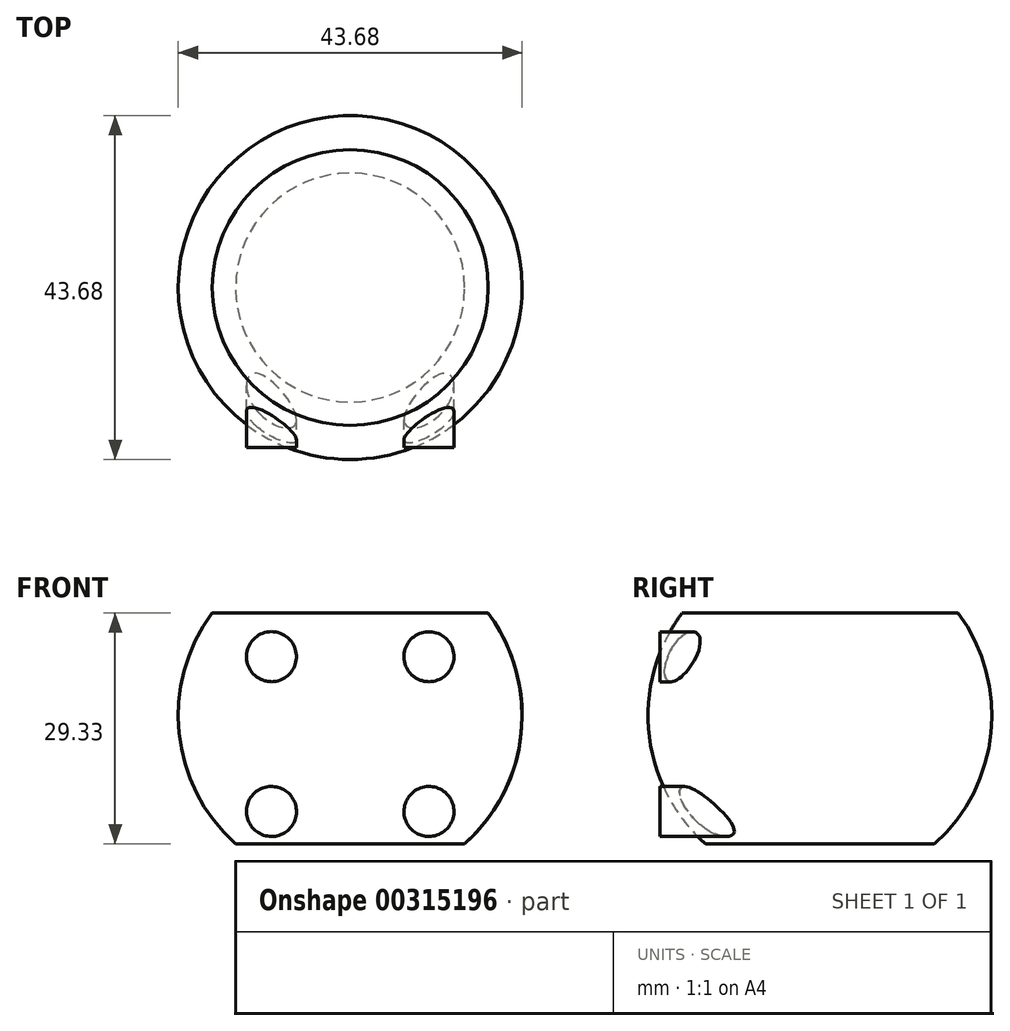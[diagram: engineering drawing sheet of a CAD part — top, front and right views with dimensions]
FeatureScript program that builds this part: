
annotation { "Feature Type Name" : "Feature", "Feature Type Description" : "" }
export const myFeature = defineFeature(function(context is Context, id is Id, definition is map)
    precondition{}
    {
        {
            var Q0;
            Q0=qCreatedBy(makeId("Front.planeOp"),FACE);
            var sketch = newSketch(context, id + "F0", { "sketchPlane" : qUnion([Q0])});
            skArc(sketch, "E0", {"start": v(-17.52, 13.04) * mm, "mid": v(-21.73, -2.2) * mm, "end": v(-14.55, -16.3) * mm});
            skLineSegment(sketch, "E1", {"start": v(-17.52, 13.04) * mm, "end": v(17.52, 13.04) * mm});
            skLineSegment(sketch, "E2", {"start": v(0, 33.05) * mm, "end": v(0, -36.53) * mm});
            skPoint(sketch, "E2.endSnap0", {"position": v(0, 13.04) * mm});
            skLineSegment(sketch, "E3", {"start": v(-14.55, -16.3) * mm, "end": v(14.55, -16.3) * mm});
            skArc(sketch, "E4.trimOffspring", {"start": v(14.55, -16.3) * mm, "mid": v(21.73, -2.2) * mm, "end": v(17.52, 13.04) * mm});
            skPoint(sketch, "E5.center.orphan", {"position": v(-8.7, -12.61) * mm});
            skPoint(sketch, "E6.center.orphan", {"position": v(8.7, -12.61) * mm});
            skSolve(sketch);
        }
        {
            var Q0;
            {var subQ1=sQuery(id+"F0.wireOp",EDGE,"E0");Q0=makeQuery(id+"F0.imprint","IMPRINT",FACE,{"disambiguationData":[TD([[makeQuery(id+"F0.imprint","IMPRINT",EDGE,{"derivedFrom":subQ1}),1.0]])]});}
            var Q1;
            Q1=sQuery(id+"F0.wireOp",EDGE,"E2");
            revolve(context, id + "F1", {"entities" : qUnion([Q0]), "axis" : qUnion([Q1]), "revolveType" : RevolveType.FULL});
        }
        {
            var Q0;
            Q0=qCreatedBy(makeId("Front.planeOp"),FACE);
            var sketch = newSketch(context, id + "F2", { "sketchPlane" : qUnion([Q0])});
            skCircle(sketch, "E7", {"center": v(-10, -12.18) * mm, "radius": 3.18 * mm});
            skCircle(sketch, "E8", {"center": v(10, -12.18) * mm, "radius": 3.18 * mm});
            skCircle(sketch, "E9", {"center": v(-10, 7.49) * mm, "radius": 3.18 * mm});
            skCircle(sketch, "E10", {"center": v(10, 7.49) * mm, "radius": 3.18 * mm});
            skSolve(sketch);
        }
        {
            var Q0;
            Q0 = qSketchRegion(id + "F2", true);
            extrude(context, id + "F3", {"entities" : qUnion([Q0]), "operationType" : NewBodyOperationType.ADD, "depth" : 20.32 * mm});
        }
    });
